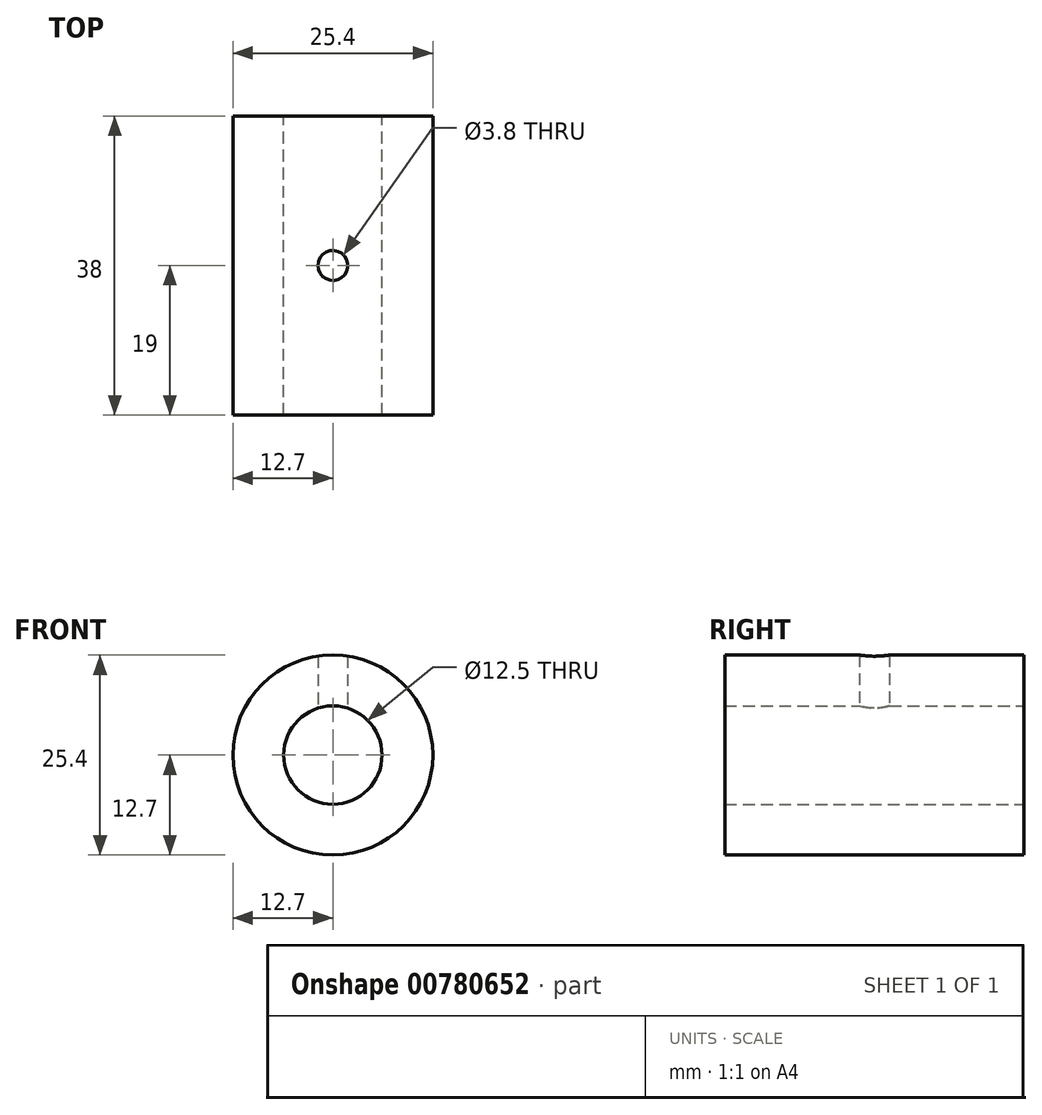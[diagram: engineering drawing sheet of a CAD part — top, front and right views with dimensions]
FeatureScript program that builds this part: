
annotation { "Feature Type Name" : "Feature", "Feature Type Description" : "" }
export const myFeature = defineFeature(function(context is Context, id is Id, definition is map)
    precondition{}
    {
        {
            var Q0;
            Q0=qCreatedBy(makeId("Front.planeOp"),FACE);
            var sketch = newSketch(context, id + "F0", { "sketchPlane" : qUnion([Q0])});
            skCircle(sketch, "E0", {"center": v(0, 0) * mm, "radius": 6.25 * mm});
            skCircle(sketch, "E1", {"center": v(0, 0) * mm, "radius": 12.7 * mm});
            skSolve(sketch);
        }
        {
            var Q0;
            Q0 = qSketchRegion(id + "F0", true);
            extrude(context, id + "F1", {"entities" : qUnion([Q0]), "endBound" : BoundingType.SYMMETRIC, "depth" : 38 * mm, "offsetDistance" : 25 * mm});
        }
        {
            var Q0;
            Q0=qCreatedBy(makeId("Top.planeOp"),FACE);
            var sketch = newSketch(context, id + "F2", { "sketchPlane" : qUnion([Q0])});
            skCircle(sketch, "E2", {"center": v(0, 0) * mm, "radius": 1.9 * mm});
            skSolve(sketch);
        }
        {
            var Q0;
            Q0 = qSketchRegion(id + "F2", true);
            var Q1;
            Q1=makeQuery(id+"F1.opExtrude","SWEPT_FACE",FACE,{"disambiguationData":[OSD([sQuery(id+"F0.wireOp",EDGE,"E1")])]});
            extrude(context, id + "F3", {"entities" : qUnion([Q0]), "operationType" : NewBodyOperationType.REMOVE, "endBound" : BoundingType.UP_TO_SURFACE, "depth" : 25 * mm, "endBoundEntityFace" : qUnion([Q1]), "offsetDistance" : 25 * mm});
        }
    });
